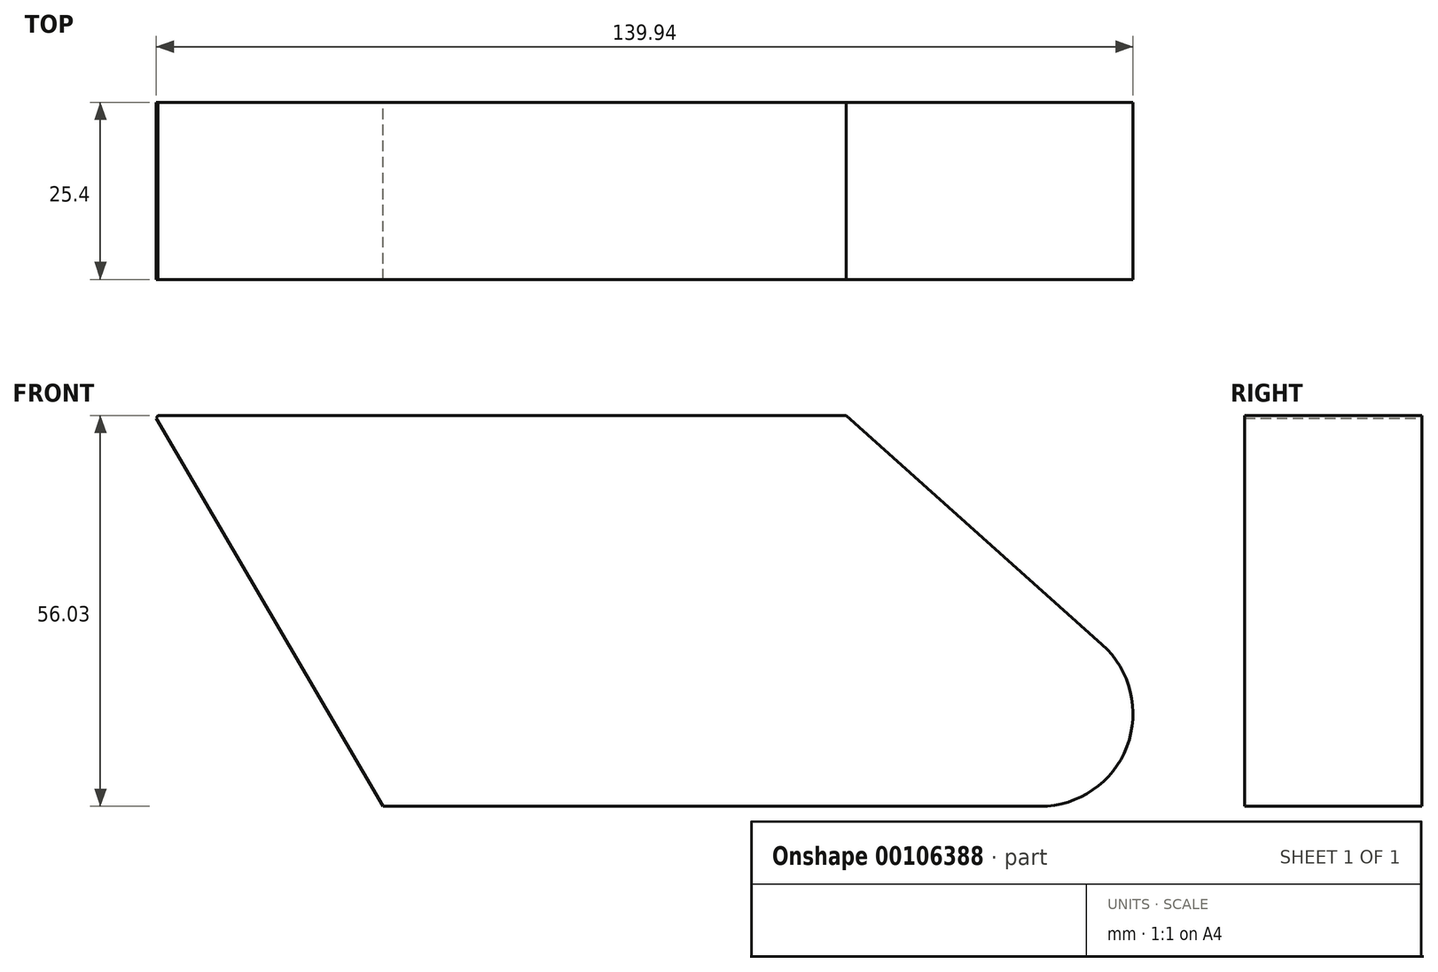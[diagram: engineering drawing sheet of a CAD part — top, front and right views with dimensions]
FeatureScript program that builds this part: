
annotation { "Feature Type Name" : "Feature", "Feature Type Description" : "" }
export const myFeature = defineFeature(function(context is Context, id is Id, definition is map)
    precondition{}
    {
        {
            var Q0;
            Q0=qCreatedBy(makeId("Front.planeOp"),FACE);
            var sketch = newSketch(context, id + "F0", { "sketchPlane" : qUnion([Q0])});
            skLineSegment(sketch, "E0", {"start": v(-66.34, -39.22) * mm, "end": v(27.8, -39.22) * mm});
            skLineSegment(sketch, "E1", {"start": v(-66.34, -39.22) * mm, "end": v(-99.06, 16.8) * mm});
            skLineSegment(sketch, "E2", {"start": v(-99.06, 16.8) * mm, "end": v(0, 16.8) * mm});
            skLineSegment(sketch, "E3", {"start": v(0, 16.8) * mm, "end": v(36.67, -16.03) * mm});
            skLineSegment(sketch, "E4", {"start": v(-94.13, 24.43) * mm, "end": v(-103.1, 9.19) * mm});
            skArc(sketch, "E5", {"start": v(27.8, -39.22) * mm, "mid": v(40.22, -30.68) * mm, "end": v(36.67, -16.03) * mm});
            skSolve(sketch);
        }
        {
            var Q0;
            {var subQ5=sQuery(id+"F0.wireOp",EDGE,"E0");Q0=makeQuery(id+"F0.imprint","IMPRINT",FACE,{"disambiguationData":[TD([[makeQuery(id+"F0.imprint","IMPRINT",EDGE,{"derivedFrom":subQ5}),1.0]])]});}
            extrude(context, id + "F1", {"entities" : qUnion([Q0]), "depth" : 25.4 * mm});
        }
    });
